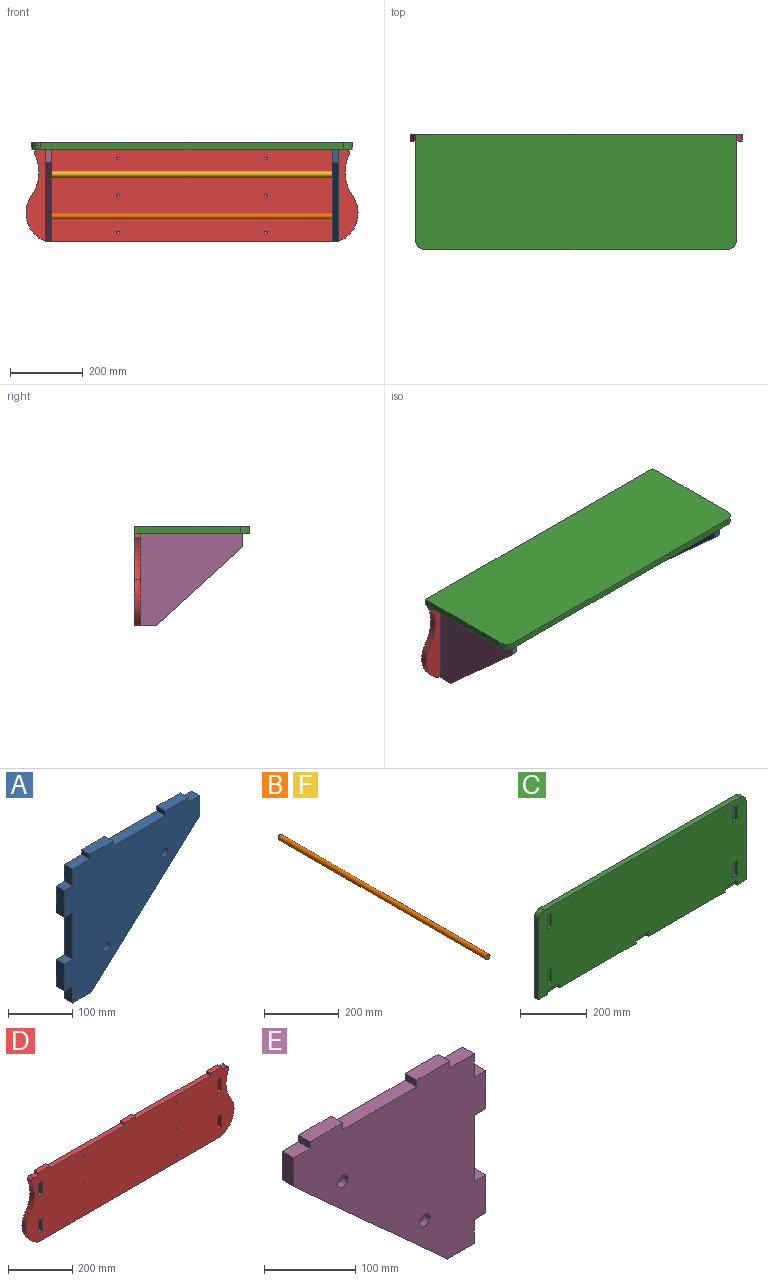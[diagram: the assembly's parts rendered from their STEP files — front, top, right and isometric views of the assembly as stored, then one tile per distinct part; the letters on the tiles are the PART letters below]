
ASSEMBLY  parts=6 mates=5
PART A: 27 faces, bbox 297.4x18x263 mm
  f0: plane 88.9x18.03mm, normal (-1,0,0), area 1603.2mm2, adj f1,f22,f23,f24
  f1: plane 18.03x18.03mm, normal (0,0,1), area 325.2mm2, adj f0,f2,f23,f24
  f2: plane 50.8x18.03mm, normal (-1,0,0), area 916.1mm2, adj f1,f3,f23,f24
  f3: plane 18.03x18.03mm, normal (0,0,-1), area 325.2mm2, adj f2,f4,f23,f24
  f4: plane 31.75x18.03mm, normal (-1,0,0), area 572.6mm2, adj f3,f5,f23,f24
  f5: plane 41.91x18.03mm, normal (0,0,-1), area 755.8mm2, adj f4,f6,f23,f24
  f6: plane 237.49x215.9mm, normal (0.67,0,-0.74), area 5788.2mm2, adj f5,f7,f23,f24
  f7: plane 38.1x18.03mm, normal (1,0,0), area 687.1mm2, adj f6,f8,f23,f24
  f8: plane 25.4x18.03mm, normal (0,0,1), area 458.1mm2, adj f7,f9,f23,f24
  f9: plane 18.03x9.02mm, normal (1,0,0), area 162.6mm2, adj f8,f10,f23,f24
  f10: plane 50.8x18.03mm, normal (0,0,1), area 916.1mm2, adj f9,f11,f23,f24
  f11: plane 18.03x9.02mm, normal (-1,0,0), area 162.6mm2, adj f10,f12,f23,f24
  f12: plane 114.3x18.03mm, normal (0,0,1), area 2061.3mm2, adj f11,f13,f23,f24
  f13: plane 18.03x9.02mm, normal (1,0,0), area 162.6mm2, adj f12,f14,f23,f24
  f14: plane 50.8x18.03mm, normal (0,0,1), area 916.1mm2, adj f13,f15,f23,f24
  f15: plane 18.03x9.02mm, normal (-1,0,0), area 162.6mm2, adj f14,f16,f23,f24
  f16: plane 38.1x18.03mm, normal (0,0,1), area 687.1mm2, adj f15,f17,f23,f24
  f17: plane 31.75x18.03mm, normal (-1,0,0), area 572.6mm2, adj f16,f18,f23,f24
  f18: plane 18.03x18.03mm, normal (0,0,1), area 325.2mm2, adj f17,f19,f23,f24
  f19: plane 50.8x18.03mm, normal (-1,0,0), area 916.1mm2, adj f18,f22,f23,f24
  f20: cylinder r=8mm len=16mm, axis (0,1,0), area 453.3mm2, adj f23,f25
  f21: cylinder r=8mm len=16mm, axis (0,1,0), area 453.3mm2, adj f23,f26
  f22: plane 18.03x18.03mm, normal (0,0,-1), area 325.2mm2, adj f0,f19,f23,f24
  f23: plane 297.43x263.02mm, normal (0,-1,0), area 47676.7mm2, adj f0,f1,f2,f3,f4,f5,f6,f7
  f24: plane 297.43x263.02mm, normal (0,1,0), area 48078.9mm2, adj f0,f1,f2,f3,f4,f5,f6,f7
  f25: plane 16x16mm, normal (0,-1,0), area 201.1mm2, adj f20
  f26: plane 16x16mm, normal (0,-1,0), area 201.1mm2, adj f21
PART B: 3 faces, bbox 16x787.4x16 mm
  f0: cylinder r=8mm len=787.4mm, axis (0,-1,0), area 39584mm2, adj f1,f2
  f1: plane 16x16mm, normal (0,1,0), area 201.1mm2, adj f0
  f2: plane 16x16mm, normal (0,-1,0), area 201.1mm2, adj f0
PART C: 40 faces, bbox 881.6x18x316.5 mm
  f0: plane 18.03x9.02mm, normal (1,0,0), area 162.6mm2, adj f1,f9,f31,f33
  f1: plane 50.8x9.02mm, normal (0,0,-1), area 458.1mm2, adj f0,f2,f31,f33
  f2: plane 18.03x9.02mm, normal (-1,0,0), area 162.6mm2, adj f1,f9,f31,f33
  f3: plane 18.03x9.02mm, normal (1,0,0), area 162.6mm2, adj f4,f9,f31,f35
  f4: plane 50.8x9.02mm, normal (0,0,-1), area 458.1mm2, adj f3,f5,f31,f35
  f5: plane 18.03x9.02mm, normal (-1,0,0), area 162.6mm2, adj f4,f9,f31,f35
  f6: plane 18.03x9.02mm, normal (1,0,0), area 162.6mm2, adj f7,f9,f31,f34
  f7: plane 50.8x9.02mm, normal (0,0,-1), area 458.1mm2, adj f6,f8,f31,f34
  f8: plane 18.03x9.02mm, normal (-1,0,0), area 162.6mm2, adj f7,f9,f31,f34
  f9: plane 881.63x18.03mm, normal (0,0,-1), area 14525.2mm2, adj f0,f2,f3,f5,f6,f8,f10,f30
  f10: plane 291.08x18.03mm, normal (1,0,0), area 5249.4mm2, adj f9,f11,f31,f32
  f11: cylinder r=25.4mm len=25.4mm, axis (0,1,0), area 719.5mm2, adj f10,f12,f31,f32
  f12: plane 830.83x18.03mm, normal (0,0,1), area 14983.3mm2, adj f11,f13,f31,f32
  f13: cylinder r=25.4mm len=25.4mm, axis (0,1,0), area 719.5mm2, adj f12,f30,f31,f32
  f14: plane 18.03x9.02mm, normal (0,0,1), area 162.6mm2, adj f15,f26,f31,f39
  f15: plane 50.8x9.02mm, normal (1,0,0), area 458.1mm2, adj f14,f16,f31,f39
  f16: plane 18.03x9.02mm, normal (0,0,-1), area 162.6mm2, adj f15,f26,f31,f39
  f17: plane 18.03x9.02mm, normal (0,0,1), area 162.6mm2, adj f18,f27,f31,f38
  f18: plane 50.8x9.02mm, normal (1,0,0), area 458.1mm2, adj f17,f19,f31,f38
  f19: plane 18.03x9.02mm, normal (0,0,-1), area 162.6mm2, adj f18,f27,f31,f38
  f20: plane 50.8x9.02mm, normal (-1,0,0), area 458.1mm2, adj f21,f28,f31,f37
  f21: plane 18.03x9.02mm, normal (0,0,1), area 162.6mm2, adj f20,f22,f31,f37
  f22: plane 50.8x9.02mm, normal (1,0,0), area 458.1mm2, adj f21,f28,f31,f37
  f23: plane 50.8x9.02mm, normal (-1,0,0), area 458.1mm2, adj f24,f29,f31,f36
  f24: plane 18.03x9.02mm, normal (0,0,1), area 162.6mm2, adj f23,f25,f31,f36
  f25: plane 50.8x9.02mm, normal (1,0,0), area 458.1mm2, adj f24,f29,f31,f36
  f26: plane 50.8x9.02mm, normal (-1,0,0), area 458.1mm2, adj f14,f16,f31,f39
  f27: plane 50.8x9.02mm, normal (-1,0,0), area 458.1mm2, adj f17,f19,f31,f38
  f28: plane 18.03x9.02mm, normal (0,0,-1), area 162.6mm2, adj f20,f22,f31,f37
  f29: plane 18.03x9.02mm, normal (0,0,-1), area 162.6mm2, adj f23,f25,f31,f36
  f30: plane 291.08x18.03mm, normal (-1,0,0), area 5249.4mm2, adj f9,f13,f31,f32
  f31: plane 881.63x316.48mm, normal (0,-1,0), area 272333.3mm2, adj f0,f1,f2,f3,f4,f5,f6,f7
  f32: plane 881.63x316.48mm, normal (0,1,0), area 278746.1mm2, adj f9,f10,f11,f12,f13,f30
  f33: plane 50.8x18.03mm, normal (0,-1,0), area 916.1mm2, adj f0,f1,f2,f9
  f34: plane 50.8x18.03mm, normal (0,-1,0), area 916.1mm2, adj f6,f7,f8,f9
  f35: plane 50.8x18.03mm, normal (0,-1,0), area 916.1mm2, adj f3,f4,f5,f9
  f36: plane 50.8x18.03mm, normal (0,-1,0), area 916.1mm2, adj f23,f24,f25,f29
  f37: plane 50.8x18.03mm, normal (0,-1,0), area 916.1mm2, adj f20,f21,f22,f28
  f38: plane 50.8x18.03mm, normal (0,-1,0), area 916.1mm2, adj f17,f18,f19,f27
  f39: plane 50.8x18.03mm, normal (0,-1,0), area 916.1mm2, adj f14,f15,f16,f26
PART D: 44 faces, bbox 912.2x18x263 mm
  f0: plane 18.03x18.03mm, normal (0,0,-1), area 325.2mm2, adj f1,f41,f42,f43
  f1: plane 50.8x18.03mm, normal (-1,0,0), area 916.1mm2, adj f0,f2,f42,f43
  f2: plane 18.03x18.03mm, normal (0,0,1), area 325.2mm2, adj f1,f41,f42,f43
  f3: plane 18.03x18.03mm, normal (0,0,1), area 325.2mm2, adj f4,f31,f42,f43
  f4: plane 50.8x18.03mm, normal (1,0,0), area 916.1mm2, adj f3,f5,f42,f43
  f5: plane 18.03x18.03mm, normal (0,0,-1), area 325.2mm2, adj f4,f31,f42,f43
  f6: plane 50.8x18.03mm, normal (1,0,0), area 916.1mm2, adj f7,f38,f42,f43
  f7: plane 18.03x18.03mm, normal (0,0,-1), area 325.2mm2, adj f6,f8,f42,f43
  f8: plane 50.8x18.03mm, normal (-1,0,0), area 916.1mm2, adj f7,f38,f42,f43
  f9: plane 50.8x18.03mm, normal (-1,0,0), area 916.1mm2, adj f10,f39,f42,f43
  f10: plane 18.03x18.03mm, normal (0,0,1), area 325.2mm2, adj f9,f11,f42,f43
  f11: plane 50.8x18.03mm, normal (1,0,0), area 916.1mm2, adj f10,f39,f42,f43
  f12: plane 18.03x9.02mm, normal (-1,0,0), area 162.6mm2, adj f13,f40,f42,f43
  f13: plane 19.05x18.03mm, normal (0,0,1), area 343.5mm2, adj f12,f14,f42,f43
  f14: cylinder r=10.94mm len=18.03mm, axis (0,1,0), area 398.3mm2, adj f13,f15,f42,f43
  f15: cylinder r=110.8mm len=111.68mm, axis (0,1,0), area 2118.7mm2, adj f14,f16,f42,f43
  f16: cylinder r=84.11mm len=126.64mm, axis (0,1,0), area 2744.1mm2, adj f15,f17,f42,f43
  f17: plane 805.43x18.03mm, normal (0,0,-1), area 14525.2mm2, adj f16,f18,f42,f43
  f18: cylinder r=84.11mm len=126.64mm, axis (0,1,0), area 2744.1mm2, adj f17,f19,f42,f43
  f19: cylinder r=110.8mm len=111.68mm, axis (0,1,0), area 2118.7mm2, adj f18,f20,f42,f43
  f20: cylinder r=10.94mm len=18.03mm, axis (0,1,0), area 398.3mm2, adj f19,f21,f42,f43
  f21: plane 19.05x18.03mm, normal (0,0,1), area 343.5mm2, adj f20,f22,f42,f43
  f22: plane 18.03x9.02mm, normal (1,0,0), area 162.6mm2, adj f21,f23,f42,f43
  f23: plane 50.8x18.03mm, normal (0,0,1), area 916.1mm2, adj f22,f24,f42,f43
  f24: plane 18.03x9.02mm, normal (-1,0,0), area 162.6mm2, adj f23,f25,f42,f43
  f25: plane 326.52x18.03mm, normal (0,0,1), area 5888.4mm2, adj f24,f26,f42,f43
  f26: plane 18.03x9.02mm, normal (1,0,0), area 162.6mm2, adj f25,f27,f42,f43
  f27: plane 50.8x18.03mm, normal (0,0,1), area 916.1mm2, adj f26,f28,f42,f43
  f28: plane 18.03x9.02mm, normal (-1,0,0), area 162.6mm2, adj f27,f29,f42,f43
  f29: plane 326.52x18.03mm, normal (0,0,1), area 5888.4mm2, adj f28,f30,f42,f43
  f30: plane 18.03x9.02mm, normal (1,0,0), area 162.6mm2, adj f29,f40,f42,f43
  f31: plane 50.8x18.03mm, normal (-1,0,0), area 916.1mm2, adj f3,f5,f42,f43
  f32: cylinder r=3.19mm len=18.03mm, axis (0,1,0), area 361.2mm2, adj f42,f43
  f33: cylinder r=3.19mm len=18.03mm, axis (0,1,0), area 361.2mm2, adj f42,f43
  f34: cylinder r=3.19mm len=18.03mm, axis (0,1,0), area 361.2mm2, adj f42,f43
  f35: cylinder r=3.19mm len=18.03mm, axis (0,1,0), area 361.2mm2, adj f42,f43
  f36: cylinder r=3.19mm len=18.03mm, axis (0,1,0), area 361.2mm2, adj f42,f43
  f37: cylinder r=3.19mm len=18.03mm, axis (0,1,0), area 361.2mm2, adj f42,f43
  f38: plane 18.03x18.03mm, normal (0,0,1), area 325.2mm2, adj f6,f8,f42,f43
  f39: plane 18.03x18.03mm, normal (0,0,-1), area 325.2mm2, adj f9,f11,f42,f43
  f40: plane 50.8x18.03mm, normal (0,0,1), area 916.1mm2, adj f12,f30,f42,f43
  f41: plane 50.8x18.03mm, normal (1,0,0), area 916.1mm2, adj f0,f2,f42,f43
  f42: plane 912.19x263.02mm, normal (0,-1,0), area 218910.9mm2, adj f0,f1,f2,f3,f4,f5,f6,f7
  f43: plane 912.19x263.02mm, normal (0,1,0), area 218910.9mm2, adj f0,f1,f2,f3,f4,f5,f6,f7
PART E: 27 faces, bbox 297.4x18x263 mm
  f0: plane 31.75x18.03mm, normal (1,0,0), area 572.6mm2, adj f1,f22,f23,f24
  f1: plane 18.03x18.03mm, normal (0,0,-1), area 325.2mm2, adj f0,f2,f23,f24
  f2: plane 50.8x18.03mm, normal (1,0,0), area 916.1mm2, adj f1,f3,f23,f24
  f3: plane 18.03x18.03mm, normal (0,0,1), area 325.2mm2, adj f2,f4,f23,f24
  f4: plane 88.9x18.03mm, normal (1,0,0), area 1603.2mm2, adj f3,f5,f23,f24
  f5: plane 18.03x18.03mm, normal (0,0,-1), area 325.2mm2, adj f4,f6,f23,f24
  f6: plane 50.8x18.03mm, normal (1,0,0), area 916.1mm2, adj f5,f7,f23,f24
  f7: plane 18.03x18.03mm, normal (0,0,1), area 325.2mm2, adj f6,f8,f23,f24
  f8: plane 31.75x18.03mm, normal (1,0,0), area 572.6mm2, adj f7,f9,f23,f24
  f9: plane 38.1x18.03mm, normal (0,0,1), area 687.1mm2, adj f8,f10,f23,f24
  f10: plane 18.03x9.02mm, normal (1,0,0), area 162.6mm2, adj f9,f11,f23,f24
  f11: plane 50.8x18.03mm, normal (0,0,1), area 916.1mm2, adj f10,f12,f23,f24
  f12: plane 18.03x9.02mm, normal (-1,0,0), area 162.6mm2, adj f11,f13,f23,f24
  f13: plane 114.3x18.03mm, normal (0,0,1), area 2061.3mm2, adj f12,f14,f23,f24
  f14: plane 18.03x9.02mm, normal (1,0,0), area 162.6mm2, adj f13,f15,f23,f24
  f15: plane 50.8x18.03mm, normal (0,0,1), area 916.1mm2, adj f14,f16,f23,f24
  f16: plane 18.03x9.02mm, normal (-1,0,0), area 162.6mm2, adj f15,f17,f23,f24
  f17: plane 25.4x18.03mm, normal (0,0,1), area 458.1mm2, adj f16,f18,f23,f24
  f18: plane 38.1x18.03mm, normal (-1,0,0), area 687.1mm2, adj f17,f19,f23,f24
  f19: plane 237.49x215.9mm, normal (-0.67,0,-0.74), area 5788.2mm2, adj f18,f22,f23,f24
  f20: cylinder r=8mm len=16mm, axis (0,1,0), area 453.3mm2, adj f23,f26
  f21: cylinder r=8mm len=16mm, axis (0,1,0), area 453.3mm2, adj f23,f25
  f22: plane 41.91x18.03mm, normal (0,0,-1), area 755.8mm2, adj f0,f19,f23,f24
  f23: plane 297.43x263.02mm, normal (0,-1,0), area 47676.7mm2, adj f0,f1,f2,f3,f4,f5,f6,f7
  f24: plane 297.43x263.02mm, normal (0,1,0), area 48078.9mm2, adj f0,f1,f2,f3,f4,f5,f6,f7
  f25: plane 16x16mm, normal (0,-1,0), area 201.1mm2, adj f21
  f26: plane 16x16mm, normal (0,-1,0), area 201.1mm2, adj f20
PART F: same geometry as B
PLACE A rot(axis=(0,0,-1),90deg) t=(776.12,1449.66,-187.07)mm
PLACE B rot(axis=(0.71,0.71,0),180deg) t=(-20.3,789.26,-187.07)mm
PLACE C rot(axis=(1,0,0),90deg) t=(-20.3,709.37,-42.03)mm
PLACE D t=(-20.3,506.17,-187.07)mm fixed
PLACE E rot(axis=(0,0,1),90deg) t=(-29.32,662.26,-187.07)mm
PLACE F rot(axis=(0.58,0.58,-0.58),120deg) t=(-20.3,342.67,-506.66)mm
MATE fastened D.f42 <-> A.f0  axis (0,-1,0) through (767.1,488.14,-142.62)mm
MATE fastened C.f35 <-> D.f27  axis (0,0,-1) through (373.4,497.16,-51.05)mm
MATE fastened E.f20 <-> B.f0  axis (1,0,0) through (-20.3,411.94,-244.79)mm
MATE fastened E.f21 <-> F.f0  axis (1,0,0) through (-20.3,284.94,-129.34)mm
MATE fastened D.f42 <-> E.f4  axis (0,-1,0) through (-20.3,488.14,-142.62)mm
